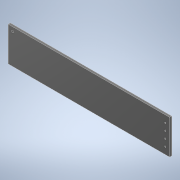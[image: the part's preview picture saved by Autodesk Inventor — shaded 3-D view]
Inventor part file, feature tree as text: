
AUTODESK INVENTOR PART (.ipt)
format: ipt  version: 2022 (Build 260153000, 153)  size: 123,904 bytes
history: native  units: mm
features: extrude x3, sketch x3, other x1
ambient origin geometry x8: Origin, YZ Plane, XZ Plane, XY Plane, X Axis, Y Axis, Z Axis, Center Point
bodies: Body1 (feature_tree)
feature tree (7):
  other  "Sólido1"
  extrude  "Extrusión1"  Depth=160.0mm
  extrude  "Extrusión2"  Depth=10.0mm
  extrude  "Extrusión4"  Depth=10.0mm
  sketch  "Boceto1"  dims[d0=750.0mm d1=160.0mm]
  sketch  "Boceto2"  dims[d2=10.0mm d3=0.0mm d4=40.0mm]
  sketch  "Boceto4"  dims[d5=40.0mm d6=10.0mm d7=10.0mm d8=0.0mm d13=20.0mm d14=32.0mm d15=32.0mm d16=32.0mm d17=32.0mm d18=6.0mm d19=6.0mm d20=6.0mm d21=6.0mm d22=10.0mm d23=0.0mm]
